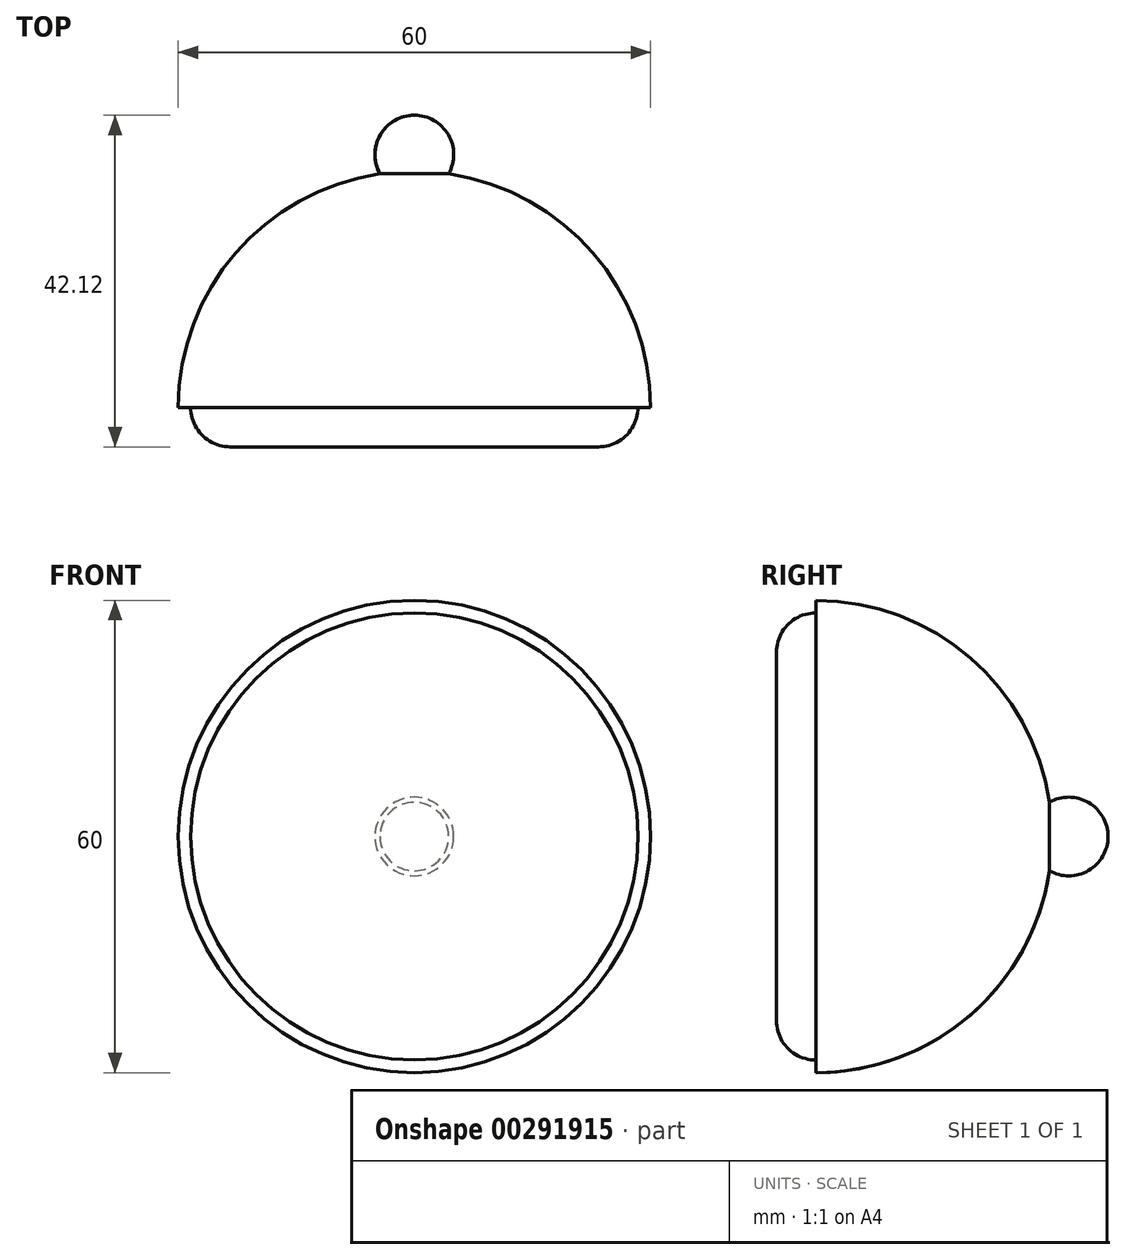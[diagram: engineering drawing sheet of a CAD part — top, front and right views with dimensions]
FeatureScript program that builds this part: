
annotation { "Feature Type Name" : "Feature", "Feature Type Description" : "" }
export const myFeature = defineFeature(function(context is Context, id is Id, definition is map)
    precondition{}
    {
        {
            var Q0;
            Q0=qCreatedBy(makeId("Top.planeOp"),FACE);
            var sketch = newSketch(context, id + "F0", { "sketchPlane" : qUnion([Q0])});
            skArc(sketch, "E0", {"start": v(-4.36, 29.68) * mm, "mid": v(-22.7, 19.61) * mm, "end": v(-30, 0) * mm});
            skLineSegment(sketch, "E1", {"start": v(0, 0) * mm, "end": v(0, 30) * mm});
            skLineSegment(sketch, "E2", {"start": v(0, 0) * mm, "end": v(-30, 0) * mm});
            skArc(sketch, "E3", {"start": v(0, 37.12) * mm, "mid": v(-4.31, 34.65) * mm, "end": v(-4.36, 29.68) * mm});
            skLineSegment(sketch, "E4", {"start": v(0, 27.12) * mm, "end": v(0, 37.12) * mm});
            skSolve(sketch);
        }
        {
            var Q0;
            Q0=makeQuery(id+"F0.imprint","IMPRINT",FACE,{"disambiguationData":[TD([[makeQuery(id+"F0.imprint","IMPRINT",EDGE,{"derivedFrom":sQuery(id+"F0.wireOp",EDGE,"E0")}),1.0]])]});
            var Q1;
            Q1=sQuery(id+"F0.wireOp",EDGE,"E1");
            revolve(context, id + "F1", {"entities" : qUnion([Q0]), "axis" : qUnion([Q1]), "revolveType" : RevolveType.FULL});
        }
        {
            var Q0;
            Q0=qCreatedBy(makeId("Front.planeOp"),FACE);
            var sketch = newSketch(context, id + "F2", { "sketchPlane" : qUnion([Q0])});
            skCircle(sketch, "E5", {"center": v(0, 0) * mm, "radius": 28.4 * mm});
            skSolve(sketch);
        }
        {
            var Q0;
            Q0=makeQuery(id+"F2.imprint","IMPRINT",FACE,{"disambiguationData":[TD([[makeQuery(id+"F2.imprint","IMPRINT",EDGE,{"derivedFrom":sQuery(id+"F2.wireOp",EDGE,"E5")}),1.0]])]});
            extrude(context, id + "F3", {"entities" : qUnion([Q0]), "operationType" : NewBodyOperationType.ADD, "depth" : 5 * mm});
        }
        {
            var Q0;
            Q0=makeQuery(id+"F3.opExtrude","CAP_EDGE",EDGE,{"disambiguationData":[OSD([sQuery(id+"F2.wireOp",EDGE,"E5")])],"isStart":false});
            fillet(context, id + "F4", {"entities" : qUnion([Q0]), "radius" : 5 * mm, "tangentPropagation" : true, "allowEdgeOverflow" : false});
        }
    });
